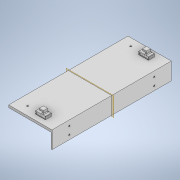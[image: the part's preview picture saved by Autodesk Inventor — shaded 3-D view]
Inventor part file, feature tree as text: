
AUTODESK INVENTOR PART (.ipt)
format: ipt  version: 2021 (Build 250183000, 183)  size: 424,448 bytes
history: native  units: mm
features: sketch x15, extrude x14, projected_geometry x11, fillet x3, hole x2, plane x2, split x1
ambient origin geometry x8: Origin, YZ Plane, XZ Plane, XY Plane, X Axis, Y Axis, Z Axis, Center Point
bodies: Solid1 (feature_tree), Solid2 (feature_tree), Solid3 (feature_tree)
feature tree (48):
  extrude  "Extrusion1"  Depth=347.0mm
  extrude  "Extrusion2"  Depth=50.0mm
  hole  "Hole1"  [1 undecoded]
  extrude  "Extrusion5"  Depth=7.5mm
  plane  "Work Plane1"
  extrude  "Extrusion6"  Depth=5.0mm TaperAngle=0.0deg
  extrude  "Extrusion7"  Depth=4.0mm
  extrude  "Extrusion8"  Depth=4.0mm
  fillet  "Fillet1"  Radius=5.0mm
  extrude  "Extrusion10"  Depth=12.0mm
  hole  "Hole3"  [1 undecoded]
  fillet  "Fillet2"  Radius=4.0mm
  extrude  "Extrusion13"  Depth=2.0mm
  extrude  "Extrusion14"  Depth=8.0mm
  extrude  "Extrusion15"  Depth=30.0mm
  extrude  "Extrusion16"  Depth=18.5mm
  fillet  "Fillet3"  Radius=30.0mm
  plane  "Work Plane2"
  split  "Split1"
  extrude  "Extrusion9"  TaperAngle=0.0deg  [1 undecoded]
  extrude  "Extrusion11"  Depth=15.0mm
  extrude  "Extrusion12"  Depth=50.0mm
  sketch  "Sketch1"  dims[d0=126.0mm d1=347.0mm]
  sketch  "Sketch2"  dims[d2=7.0mm d3=0.0mm d4=50.0mm]
  projected_geometry  "Projected Loop1"
  sketch  "Sketch4"  dims[d5=2.5mm d6=0.0mm d10=300.0mm]
  projected_geometry  "Projected Loop2"
  sketch  "Sketch7"  dims[d11=30.0mm]
  projected_geometry  "Projected Loop10"
  sketch  "Sketch8"  dims[d12=4.5mm d13=6.0mm d14=4.0mm d15=2.0mm d16=90.0deg d17=8.0mm d18=20.594885mm d35=7.5mm]
  projected_geometry  "Projected Loop11"
  sketch  "Sketch9"  dims[d36=7.5mm d37=5.0mm d38=0.0mm]
  projected_geometry  "Projected Loop12"
  projected_geometry  "Projected Loop13"
  sketch  "Sketch10"  dims[d39=48.0mm d40=4.0mm]
  projected_geometry  "Projected Loop14"
  projected_geometry  "Projected Loop15"
  sketch  "Sketch11"  dims[d41=12.0mm d42=4.0mm d43=12.0mm d44=48.0mm d45=5.0mm d46=0.0mm]
  sketch  "Sketch12"  dims[d47=12.0mm d48=12.0mm]
  sketch  "Sketch13"  dims[d49=4.0mm d50=0.0mm d51=4.0mm d52=4.0mm]
  sketch  "Sketch14"  dims[d53=1.0mm d54=0.0mm d55=2.0mm]
  sketch  "Sketch15"  dims[d57=0.0mm d58=0.0mm d59=8.0mm]
  sketch  "Sketch16"  dims[d60=18.5mm d61=30.0mm]
  projected_geometry  "Projected Loop16"
  sketch  "Sketch17"  dims[d62=10.0mm d63=0.0mm d64=18.5mm d65=30.0mm]
  projected_geometry  "Projected Loop17"
  sketch  "Sketch18"  dims[d66=10.0mm d67=0.0mm d68=0.0mm d69=0.0mm d70=15.0mm d71=50.0mm d72=12.5mm d73=50.0mm d74=50.0mm d75=50.0mm d76=4.5mm d77=6.0mm d78=7.5mm d79=2.0mm d80=90.0deg d81=8.0mm d82=20.594885mm d83=2.0mm d84=2.0mm d85=2.0mm d86=2.0mm d87=2.0mm d88=7.0mm d89=0.0mm d90=7.0mm d91=0.0mm d92=7.0mm d93=0.0mm d94=7.0mm d95=0.0mm d96=1.0mm d97=-173.5mm]
  projected_geometry  "Projected Loop18"
note: 3 required parameter values undecoded (feature->parameter linkage not recoverable at this tier; creation-order binding heuristic only, values carry confidence <= 0.55)
